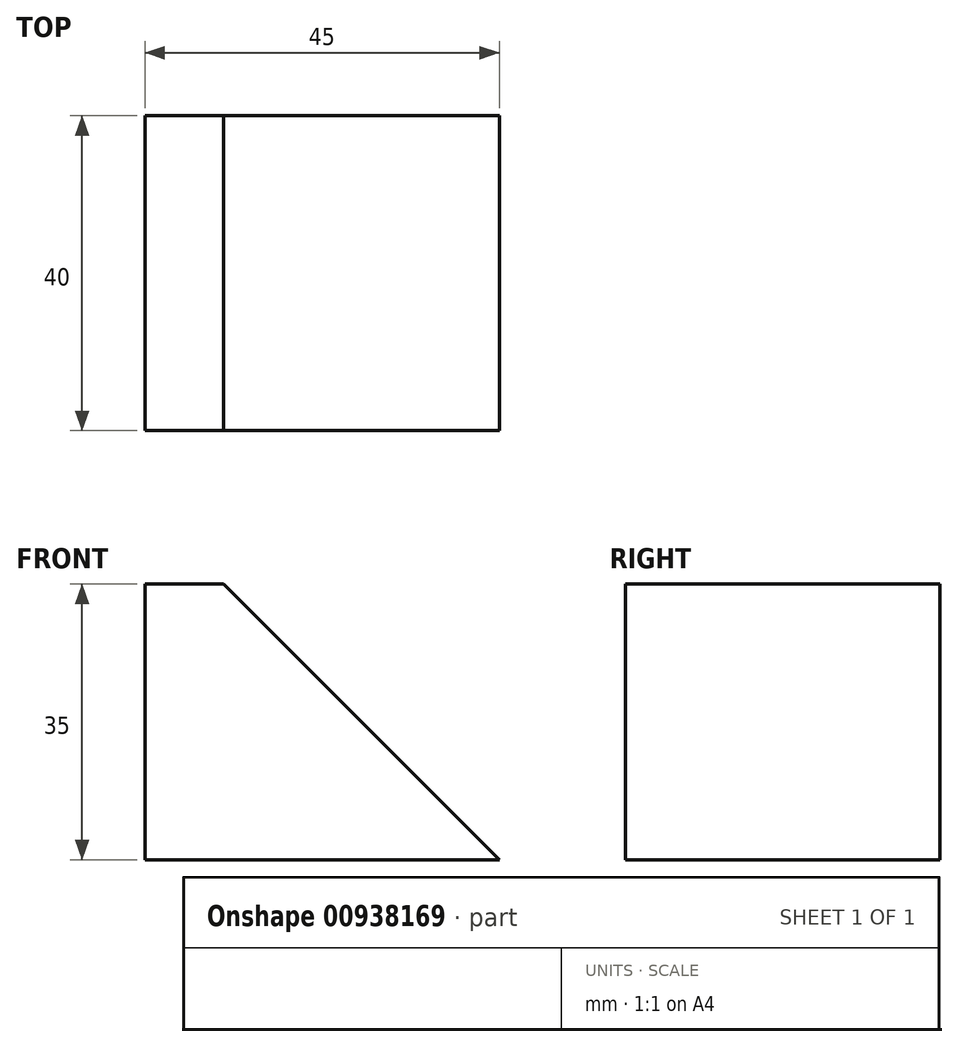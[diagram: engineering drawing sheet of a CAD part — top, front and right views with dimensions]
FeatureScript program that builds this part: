
annotation { "Feature Type Name" : "Feature", "Feature Type Description" : "" }
export const myFeature = defineFeature(function(context is Context, id is Id, definition is map)
    precondition{}
    {
        {
            var Q0;
            Q0=qCreatedBy(makeId("Front.planeOp"),FACE);
            var sketch = newSketch(context, id + "F0", { "sketchPlane" : qUnion([Q0])});
            skLineSegment(sketch, "E0.bottom", {"start": v(22.5, -17.5) * mm, "end": v(-22.5, -17.5) * mm});
            skLineSegment(sketch, "E0.top", {"start": v(-12.5, 17.5) * mm, "end": v(-22.5, 17.5) * mm});
            skLineSegment(sketch, "E0.right", {"start": v(-22.5, -17.5) * mm, "end": v(-22.5, 17.5) * mm});
            skPoint(sketch, "E0.middle", {"position": v(0, 0) * mm});
            skLineSegment(sketch, "E1", {"start": v(22.5, -17.5) * mm, "end": v(-12.5, 17.5) * mm});
            skPoint(sketch, "E0.left.end.orphan", {"position": v(22.5, 17.5) * mm});
            skSolve(sketch);
        }
        {
            var Q0;
            Q0 = qSketchRegion(id + "F0", true);
            extrude(context, id + "F1", {"entities" : qUnion([Q0]), "depth" : 40 * mm, "offsetDistance" : 25 * mm});
        }
    });
